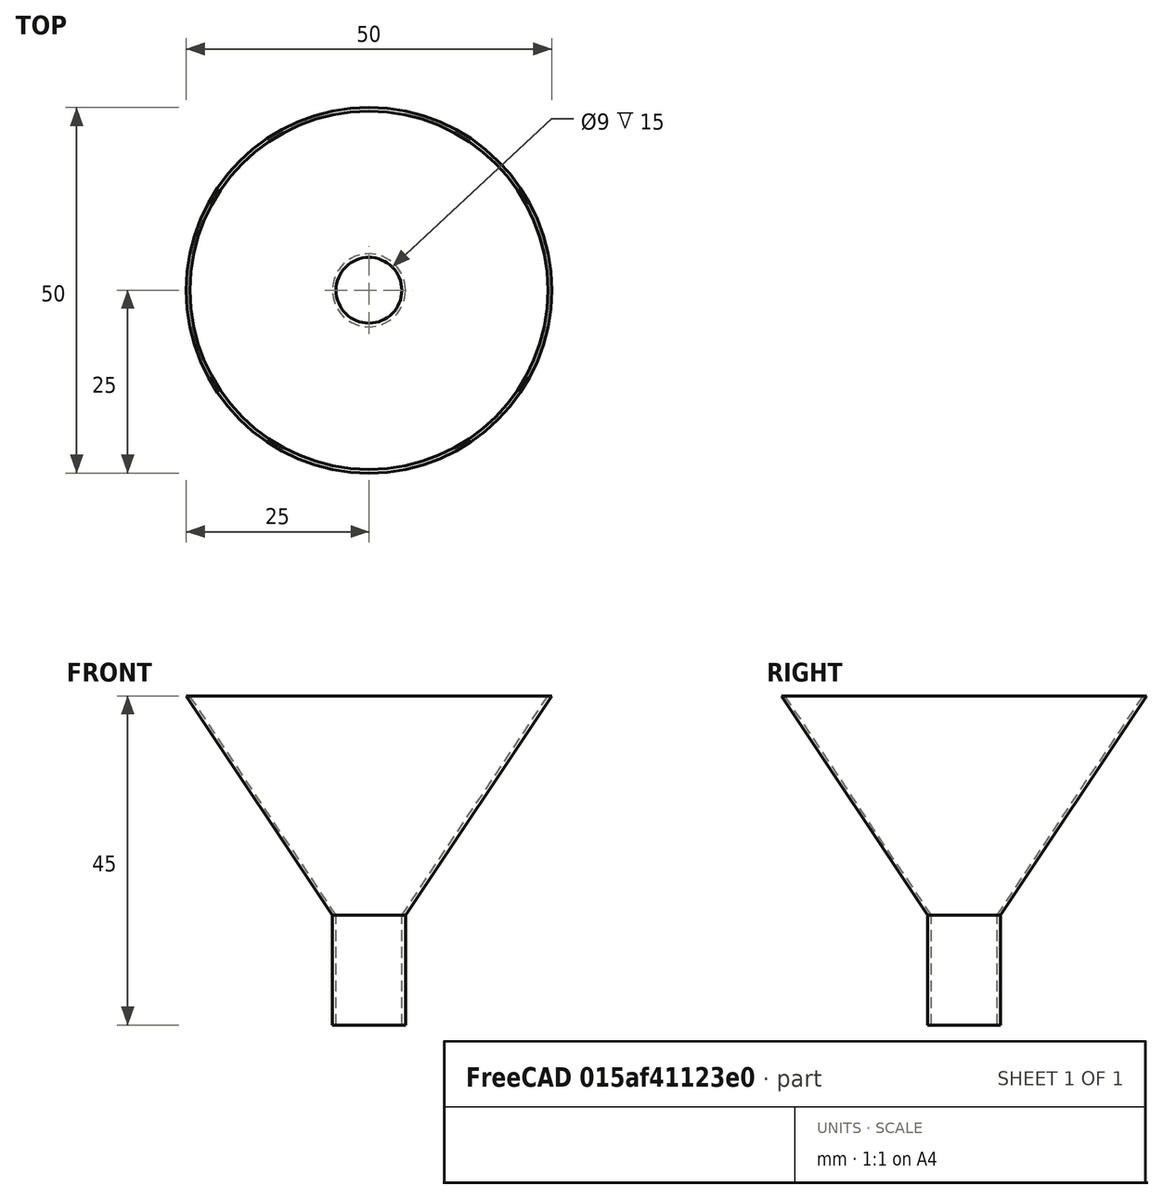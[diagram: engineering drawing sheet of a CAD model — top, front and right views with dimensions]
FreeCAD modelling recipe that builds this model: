
FCSTD DOCUMENT  (FreeCAD 0.18.4R)
Label: tutorial_freecad_ex14_d
License: All rights reserved
LicenseURL: http://en.wikipedia.org/wiki/All_rights_reserved
objects: Part::Cylinder×2, Part::Cone×2, Part::Cut×2, Part::MultiFuse×1
note: 7 computed .brp shape members not serialized (recipe doc carries the construction recipe); baked Part::Feature solids carry a one-line shape summary decoded from their .brp

FEATURE [Part::Cylinder] Cylinder  label="cilindro_externo"
  Angle = 360
  AttacherType = Attacher::AttachEngine3D
  Height = 15
  Radius = 5
FEATURE [Part::Cylinder] Cylinder001  label="cilindro_interno"
  Angle = 360
  AttacherType = Attacher::AttachEngine3D
  Height = 15
  Radius = 4.5
FEATURE [Part::Cone] Cone  label="cono_exterior"
  Angle = 360
  AttacherType = Attacher::AttachEngine3D
  Height = 30
  Radius1 = 5
  Radius2 = 25
FEATURE [Part::Cone] Cone001  label="cono_interior"
  Angle = 360
  AttacherType = Attacher::AttachEngine3D
  Height = 30
  Radius1 = 4.5
  Radius2 = 24.5
FEATURE [Part::Cut] Cut001  label="cono"
  Base = -> Cone
  Placement = pos=(0,0,15) rot=(0,0,1;0rad)
  Refine = true
  Tool = -> Cone001
FEATURE [Part::Cut] Cut  label="cilindro"
  Base = -> Cylinder
  Refine = true
  Tool = -> Cylinder001
FEATURE [Part::MultiFuse] Fusion  label="fonil"
  Refine = true
  Shapes = -> [Cut001,Cut]
